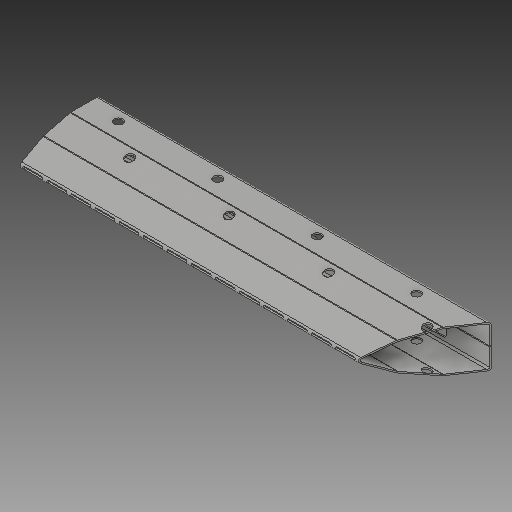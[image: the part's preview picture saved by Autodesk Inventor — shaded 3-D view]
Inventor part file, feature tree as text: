
AUTODESK INVENTOR PART (.ipt)
format: ipt  version: 2018 (Build 220112000, 112)  size: 866,304 bytes
history: native  units: mm
features: reference x24, other x23, sketch x16, sheet_metal_op x13, plane x9, projected_geometry x8, extrude x6
ambient origin geometry x8: Origin, YZ Plane, XZ Plane, XY Plane, X Axis, Y Axis, Z Axis, Center Point
bodies: Solid1 (feature_tree)
feature tree (99):
  plane  "Work Plane1"
  sheet_metal_op  "Face1"
  plane  "Work Plane2"
  sheet_metal_op  "Face2"
  plane  "Work Plane3"
  sheet_metal_op  "Face3"
  plane  "Work Plane4"
  sheet_metal_op  "Face4"
  plane  "Work Plane5"
  sheet_metal_op  "Face5"
  plane  "Work Plane6"
  sheet_metal_op  "Face6"
  plane  "Work Plane7"
  sheet_metal_op  "Face7"
  other  "midtplan"
  extrude  "afskær bund"  Depth=5.0mm
  extrude  "afskær top"  Depth=2.0mm
  extrude  "hulsæt til stifter"  Depth=5.0mm
  sketch  "Sketch14"  dims[d16=5.0mm]
  plane  "Work Plane12"
  extrude  "balusterhul"  Depth=4.0mm
  extrude  "balusterhul skråkompensering"  Depth=8.0mm
  extrude  "test"  Depth=5.0mm
  sketch  "Sketch1"  dims[d0=4.0mm d1=5.0mm]
  reference  "Reference1"
  reference  "Reference2"
  reference  "Reference3"
  reference  "Reference4"
  other  "Plate1"
  sketch  "Sketch2"  dims[d2=4.0mm d3=2.0mm]
  reference  "Reference5"
  reference  "Reference6"
  reference  "Reference7"
  reference  "Reference8"
  other  "Plate2"
  sheet_metal_op  "Bend1"
  sketch  "Sketch3"  dims[d4=8.0mm d5=5.0mm]
  reference  "Reference9"
  reference  "Reference10"
  reference  "Reference11"
  other  "Plate3"
  sheet_metal_op  "Bend2"
  sketch  "Sketch4"  dims[d6=5.0mm d7=4.0mm]
  reference  "Reference12"
  reference  "Reference13"
  reference  "Reference14"
  reference  "Reference15"
  other  "Plate4"
  sheet_metal_op  "Bend3"
  sketch  "Sketch5"  dims[d8=2.0mm d9=8.0mm]
  reference  "Reference16"
  reference  "Reference17"
  reference  "Reference18"
  other  "Plate5"
  sheet_metal_op  "Bend4"
  sketch  "Sketch6"  dims[d10=5.0mm d11=5.0mm]
  reference  "Reference19"
  reference  "Reference20"
  reference  "Reference21"
  other  "Plate6"
  sheet_metal_op  "Bend5"
  sketch  "Sketch7"  dims[d12=4.0mm]
  reference  "Reference22"
  reference  "Reference23"
  other  "Plate7"
  sheet_metal_op  "Bend6"
  sketch  "Sketch8"  dims[d13=2.0mm]
  reference  "Reference24"
  projected_geometry  "Projected Loop1"
  other  "huller til stifter"
  projected_geometry  "Projected Loop3"
  sketch  "Sketch12"  dims[d14=8.0mm]
  projected_geometry  "Projected Loop4"
  sketch  "Sketch13"  dims[d15=5.0mm]
  projected_geometry  "Projected Loop5"
  plane  "Work Plane11"
  sketch  "Sketch15"  dims[d17=4.0mm]
  sketch  "Sketch16"  dims[d18=2.0mm]
  projected_geometry  "Projected Loop6"
  projected_geometry  "Projected Loop7"
  sketch  "Sketch17"  dims[d19=8.0mm]
  projected_geometry  "Projected Loop8"
  projected_geometry  "Projected Loop9"
  sketch  "Sketch18"  dims[d20=5.0mm]
  sketch  "Sketch20"  dims[d21=5.0mm d22=4.0mm d23=2.0mm d24=8.0mm d25=5.0mm d26=5.0mm d27=4.0mm d28=2.0mm d29=8.0mm d30=5.0mm d31=4.0mm d32=0.0mm d33=3.0mm d39=250.0mm d41=33.7mm d42=33.7mm d43=60.0mm d44=70.0mm d45=16.85mm d46=65.0mm d47=60.0mm d48=10.0mm d49=0.0mm d50=250.0mm d51=33.7mm d52=33.7mm d53=60.0mm d54=16.85mm d55=65.0mm d56=60.0mm d57=30.0mm d59=302.736671mm d60=10.0mm d62=10.0mm d65=302.736671mm d66=195.343893mm d68=306.228mm d69=10.0mm d70=0.0mm d71=96.671937mm d74=10.0mm d75=0.0mm d76=5.986479mm d77=26.6mm d78=25.8mm d79=26.6mm d80=26.6mm d81=26.6mm d82=26.6mm d83=26.6mm d84=26.6mm d85=40.001254mm d95=113.170852mm d96=56.585426mm d97=90.0deg d98=49.5mm d99=100.0mm d100=0.0mm d101=2.728615mm d102=1.364307mm d103=10.0mm d104=0.0mm d105=90.0mm d106=342.765mm d107=342.765mm d108=30.0mm d109=30.0mm d110=30.0mm d111=342.765mm d112=10.0mm d113=4.0mm d114=0.0mm d115=6.0mm d116=61.0mm d117=8.0mm d118=150.0mm d120=73.2mm d121=10.0mm d123=10.0mm d125=4.0mm d126=0.0mm d129=10.0mm d130=0.0mm]
  other  "Cut1"
  other  "plantehuller"
  other  "bukkeperforering"
  parser-record x4  (decoder bookkeeping rows leaked as tree rows — omitted from the tree; the rows remain in map.json)
  other  "modul top.iam"
  other  "model:1"
  other  "Definition1"
  other  "modul.iam"
  other  "søjle+vange.iam"
  other  "stilladssøjle:2"
  other  "rør:1"
note: 4 file-system paths scrubbed to <path> (originals preserved in map.json)
